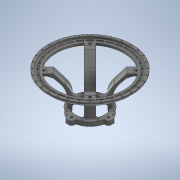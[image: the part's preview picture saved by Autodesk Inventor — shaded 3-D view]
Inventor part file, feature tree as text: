
AUTODESK INVENTOR PART (.ipt)
format: ipt  version: 2020 (Build 240168000, 168)  size: 2,105,856 bytes
history: native  units: mm
features: projected_geometry x28, other x26, sketch x23, extrude x13, revolve x9, fillet x8, pattern_circular x6, loft x6, mirror x3, chamfer x2
ambient origin geometry x8: Origin, YZ Plane, XZ Plane, XY Plane, X Axis, Y Axis, Z Axis, Center Point
bodies: Body1 (feature_tree)
feature tree (124):
  other  "Твердое тело1"
  extrude  "Выдавливание1"  Depth=34.0mm
  other  "РабПлоскость1"
  other  "РабОсь1"
  revolve  "Вращение1"
  extrude  "Выдавливание2"  Depth=45.0mm
  other  "РабТочка2"
  other  "РабТочка3"
  other  "РабТочка4"
  other  "РабПлоскость2"
  sketch  "Эскиз5"
  revolve  "Вращение2"
  revolve  "Вращение3"
  pattern_circular  "Круговой массив1"  Angle=45.0deg  [1 undecoded]
  extrude  "Выдавливание3"  Depth=2.9mm
  revolve  "Вращение4"
  fillet  "Сопряжение1"  Radius=9.0mm
  revolve  "Вращение5"
  other  "РабПлоскость6"
  other  "РабПлоскость7"
  sketch  "Эскиз10"
  revolve  "Вращение6"
  revolve  "Вращение7"
  sketch  "Эскиз11"
  sketch  "Эскиз12"
  loft  "Лофт2"
  loft  "Лофт3"
  fillet  "Сопряжение2"  Radius=1.0mm
  extrude  "Выдавливание4"  Depth=22.0mm
  loft  "Лофт4"
  fillet  "Сопряжение3"  Radius=5.0mm
  pattern_circular  "Круговой массив2"  [2 undecoded]
  revolve  "Вращение8"
  revolve  "Вращение9"
  extrude  "Выдавливание5"  Depth=2.5mm
  extrude  "Выдавливание6"  Depth=45.0mm
  pattern_circular  "Круговой массив3"  [2 undecoded]
  other  "РабПлоскость8"
  extrude  "Выдавливание8"  Depth=2.0mm
  extrude  "Выдавливание7"  Depth=2.0mm
  loft  "Лофт5"
  pattern_circular  "Круговой массив4"  Angle=45.0deg  [1 undecoded]
  fillet  "Сопряжение4"  [1 undecoded]
  chamfer  "Фаска1"  Distance=3.0mm
  sketch  "Эскиз23"
  extrude  "Выдавливание9"  TaperAngle=135.0deg  [1 undecoded]
  loft  "Лофт6"
  other  "РабПлоскость9"
  mirror  "Зеркальное отражение1"
  pattern_circular  "Круговой массив5"  [2 undecoded]
  extrude  "Выдавливание10"  TaperAngle=0.0deg  [1 undecoded]
  pattern_circular  "Круговой массив6"  [2 undecoded]
  other  "board plane"
  sketch  "Эскиз26"
  extrude  "Выдавливание11"  Depth=10.0mm
  extrude  "Выдавливание12"  Depth=2.0mm
  other  "РабПлоскость11"
  sketch  "Эскиз28"
  other  "РабПлоскость12"
  loft  "Лофт9"
  other  "РабПлоскость13"
  extrude  "Выдавливание13"  TaperAngle=45.0deg  [1 undecoded]
  chamfer  "Фаска2"  Distance=2.5mm
  other  "РабПлоскость15"
  mirror  "Зеркальное отражение6"
  mirror  "Зеркальное отражение7"
  fillet  "Сопряжение8"  [1 undecoded]
  fillet  "Сопряжение9"  [1 undecoded]
  fillet  "Сопряжение10"  Radius=40.0mm
  fillet  "Сопряжение11"  Radius=78.0mm
  sketch  "Эскиз1"
  sketch  "Эскиз2"
  sketch  "Эскиз4"
  projected_geometry  "Спроецированная петля1"
  projected_geometry  "Спроецированная петля2"
  projected_geometry  "Спроецированная петля3"
  other  "РабПлоскость3"
  other  "РабПлоскость4"
  other  "РабПлоскость5"
  sketch  "Эскиз6"
  sketch  "Эскиз7"
  sketch  "Эскиз9"
  projected_geometry  "Спроецированная петля4"
  projected_geometry  "Спроецированная петля5"
  other  "Ребра2"
  other  "Ребра3"
  sketch  "Эскиз13"
  projected_geometry  "Спроецированная петля6"
  projected_geometry  "Спроецированная петля7"
  sketch  "Эскиз14"
  projected_geometry  "Спроецированная петля8"
  projected_geometry  "Спроецированная петля9"
  projected_geometry  "Спроецированная петля10"
  sketch  "Эскиз16"
  sketch  "Эскиз17"
  projected_geometry  "Спроецированная петля12"
  projected_geometry  "Спроецированная петля13"
  sketch  "Эскиз18"
  sketch  "Эскиз19"
  projected_geometry  "Спроецированная петля14"
  projected_geometry  "Спроецированная петля15"
  other  "Ребра5"
  sketch  "Эскиз22"
  projected_geometry  "Спроецированная петля16"
  projected_geometry  "Спроецированная петля17"
  projected_geometry  "Спроецированная петля18"
  projected_geometry  "Спроецированная петля19"
  projected_geometry  "Спроецированная петля20"
  sketch  "Эскиз24"
  other  "Ребра6"
  sketch  "Эскиз25"
  projected_geometry  "Спроецированная петля21"
  projected_geometry  "Спроецированная петля22"
  projected_geometry  "Спроецированная петля23"
  projected_geometry  "Спроецированная петля24"
  projected_geometry  "Спроецированная петля27"
  projected_geometry  "Спроецированная петля28"
  projected_geometry  "Спроецированная петля29"
  projected_geometry  "Спроецированная петля30"
  sketch  "Эскиз29"
  other  "Ребра15"
  projected_geometry  "Спроецированная петля31"
  other  "Ребра18"
  other  "Ребра19"
note: 16 required parameter values undecoded (feature->parameter linkage not recoverable at this tier; creation-order binding heuristic only, values carry confidence <= 0.55)
